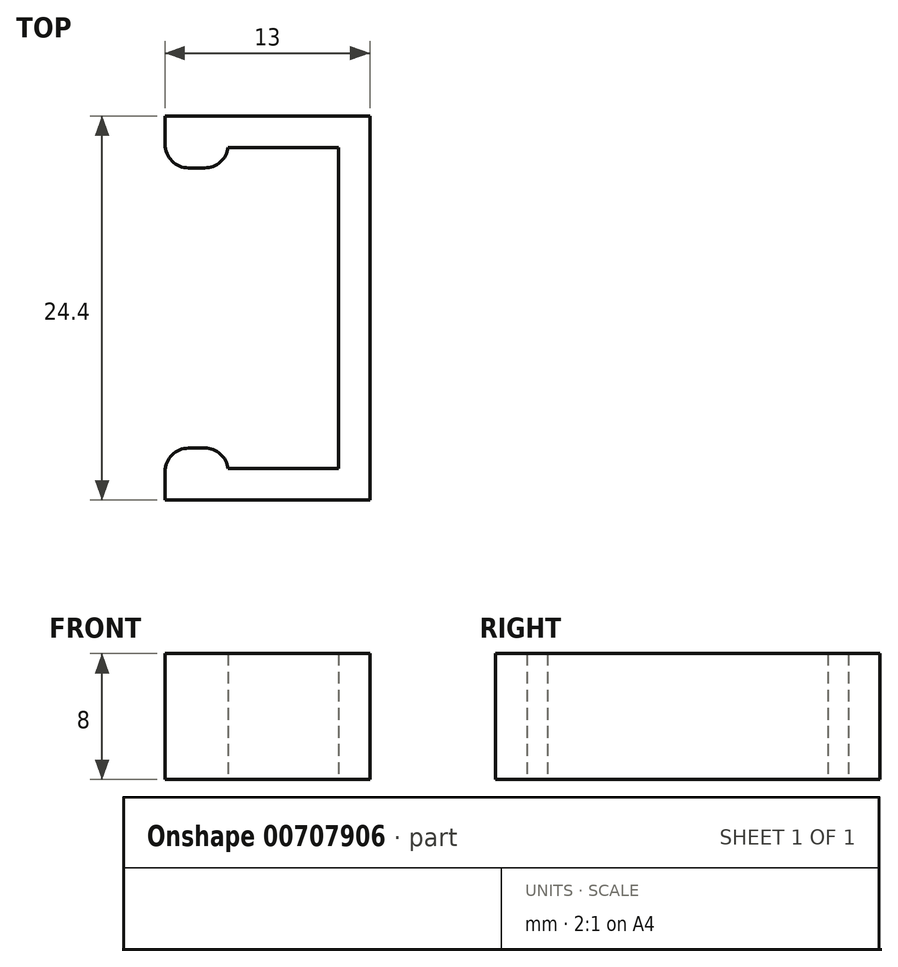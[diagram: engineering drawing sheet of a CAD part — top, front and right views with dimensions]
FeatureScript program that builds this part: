
annotation { "Feature Type Name" : "Feature", "Feature Type Description" : "" }
export const myFeature = defineFeature(function(context is Context, id is Id, definition is map)
    precondition{}
    {
        {
            var Q0;
            Q0=qCreatedBy(makeId("Top.planeOp"),FACE);
            var sketch = newSketch(context, id + "F0", { "sketchPlane" : qUnion([Q0])});
            skLineSegment(sketch, "E0", {"start": v(0, 10.2) * mm, "end": v(-7, 10.2) * mm});
            skLineSegment(sketch, "E1", {"start": v(-7, 10.2) * mm, "end": v(-7, 8.9) * mm});
            skLineSegment(sketch, "E2", {"start": v(-7, 8.9) * mm, "end": v(-11, 8.9) * mm});
            skLineSegment(sketch, "E3", {"start": v(-11, 8.9) * mm, "end": v(-11, 12.2) * mm});
            skLineSegment(sketch, "E4", {"start": v(-11, 12.2) * mm, "end": v(2, 12.2) * mm});
            skLineSegment(sketch, "E5", {"start": v(2, 12.2) * mm, "end": v(2, 0) * mm});
            skLineSegment(sketch, "E6", {"start": v(0, 10.2) * mm, "end": v(0, 0) * mm});
            skLineSegment(sketch, "E7.MirrorCS", {"start": v(-7, -10.2) * mm, "end": v(-7, -8.9) * mm});
            skLineSegment(sketch, "E8.MirrorCS", {"start": v(0, -10.2) * mm, "end": v(-7, -10.2) * mm});
            skLineSegment(sketch, "E9.MirrorCS", {"start": v(-7, -8.9) * mm, "end": v(-11, -8.9) * mm});
            skLineSegment(sketch, "E10.MirrorCS", {"start": v(0, -10.2) * mm, "end": v(0, 0) * mm});
            skLineSegment(sketch, "E11.MirrorCS", {"start": v(-11, -8.9) * mm, "end": v(-11, -12.2) * mm});
            skLineSegment(sketch, "E12.MirrorCS", {"start": v(2, -12.2) * mm, "end": v(2, 0) * mm});
            skLineSegment(sketch, "E13.MirrorCS", {"start": v(-11, -12.2) * mm, "end": v(2, -12.2) * mm});
            skSolve(sketch);
        }
        {
            var Q0;
            Q0 = qSketchRegion(id + "F0", true);
            extrude(context, id + "F1", {"entities" : qUnion([Q0]), "depth" : 8 * mm, "offsetDistance" : 25 * mm});
        }
        {
            var Q0;
            Q0=makeQuery(id+"F1.opExtrude","SWEPT_EDGE",EDGE,{"disambiguationData":[OSD([sQuery(id+"F0.wireOp",EDGE,"E1"),sQuery(id+"F0.wireOp",EDGE,"E2")])]});
            var Q1;
            Q1=makeQuery(id+"F1.opExtrude","SWEPT_EDGE",EDGE,{"disambiguationData":[OSD([sQuery(id+"F0.wireOp",EDGE,"E2"),sQuery(id+"F0.wireOp",EDGE,"E3")])]});
            var Q2;
            Q2=makeQuery(id+"F1.opExtrude","SWEPT_EDGE",EDGE,{"disambiguationData":[OSD([sQuery(id+"F0.wireOp",EDGE,"E7.MirrorCS"),sQuery(id+"F0.wireOp",EDGE,"E9.MirrorCS")])]});
            var Q3;
            Q3=makeQuery(id+"F1.opExtrude","SWEPT_EDGE",EDGE,{"disambiguationData":[OSD([sQuery(id+"F0.wireOp",EDGE,"E9.MirrorCS"),sQuery(id+"F0.wireOp",EDGE,"E11.MirrorCS")])]});
            fillet(context, id + "F2", {"entities" : qUnion([Q0, Q1, Q2, Q3]), "radius" : 1.5 * mm, "tangentPropagation" : true, "allowEdgeOverflow" : false});
        }
    });
